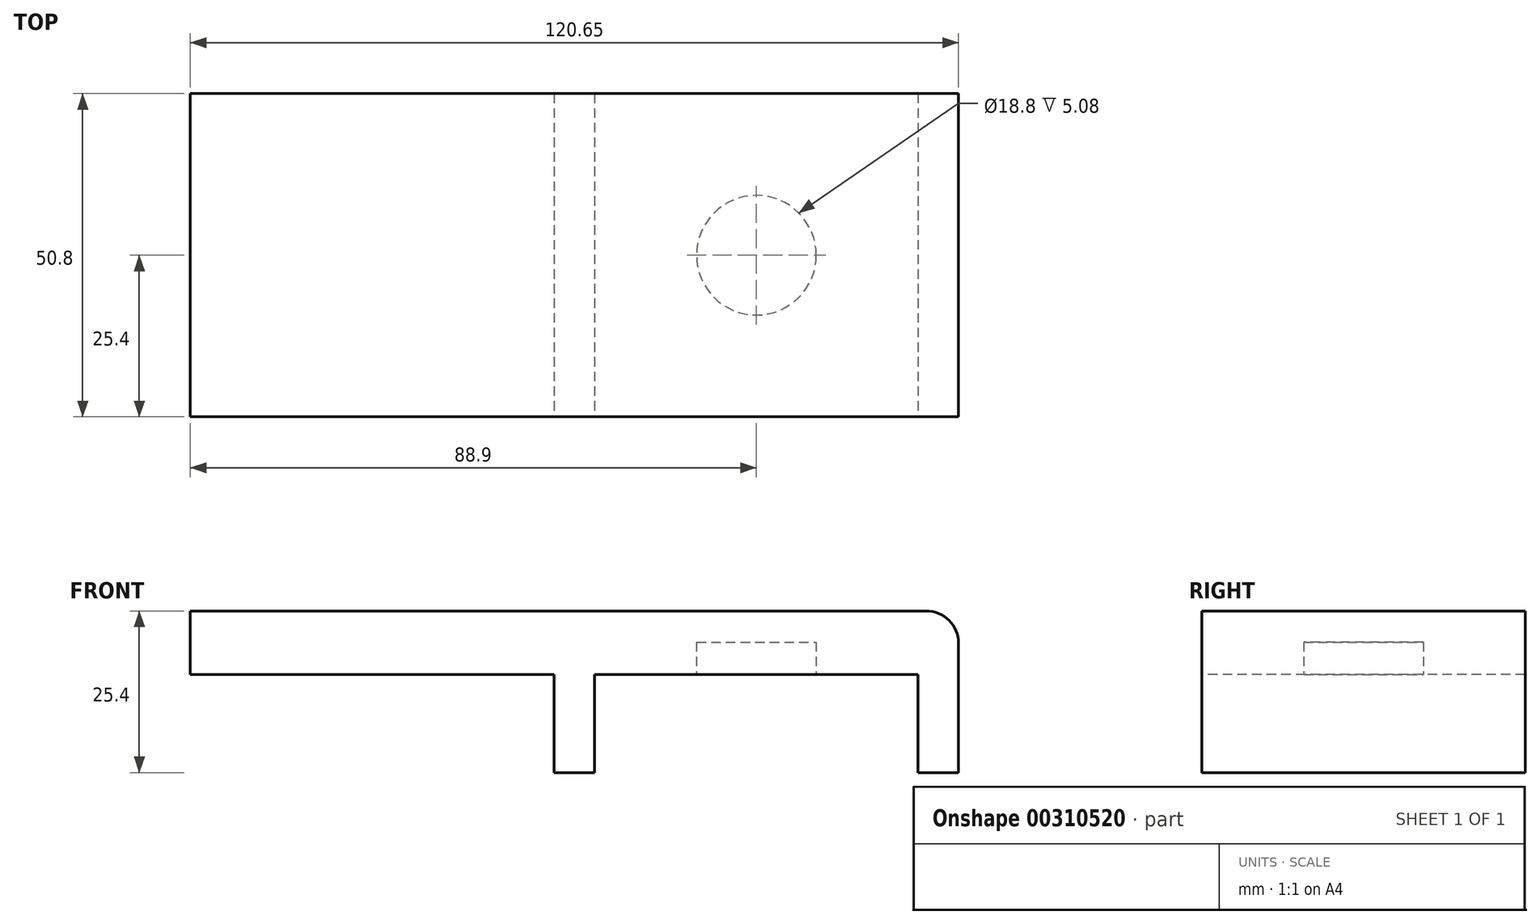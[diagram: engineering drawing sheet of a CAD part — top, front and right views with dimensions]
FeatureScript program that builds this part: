
annotation { "Feature Type Name" : "Feature", "Feature Type Description" : "" }
export const myFeature = defineFeature(function(context is Context, id is Id, definition is map)
    precondition{}
    {
        {
            var Q0;
            Q0=qCreatedBy(makeId("Front.planeOp"),FACE);
            var sketch = newSketch(context, id + "F0", { "sketchPlane" : qUnion([Q0])});
            skLineSegment(sketch, "E0.bottom", {"start": v(0, 0) * mm, "end": v(50.8, 0) * mm});
            skLineSegment(sketch, "E0.left", {"start": v(0, 0) * mm, "end": v(0, -15.44) * mm});
            skLineSegment(sketch, "E0.right", {"start": v(50.8, 0) * mm, "end": v(50.8, -15.44) * mm});
            skLineSegment(sketch, "E1.top", {"start": v(0, 9.96) * mm, "end": v(50.8, 9.96) * mm});
            skLineSegment(sketch, "E2.bottom", {"start": v(50.8, 9.96) * mm, "end": v(57.15, 9.96) * mm});
            skLineSegment(sketch, "E2.top", {"start": v(50.8, -15.44) * mm, "end": v(57.15, -15.44) * mm});
            skLineSegment(sketch, "E2.right", {"start": v(57.15, 9.96) * mm, "end": v(57.15, -15.44) * mm});
            skLineSegment(sketch, "E3.bottom", {"start": v(0, 9.96) * mm, "end": v(-6.35, 9.96) * mm});
            skLineSegment(sketch, "E3.top", {"start": v(0, -15.44) * mm, "end": v(-6.35, -15.44) * mm});
            skLineSegment(sketch, "E3.right", {"start": v(-6.35, 0) * mm, "end": v(-6.35, -15.44) * mm});
            skLineSegment(sketch, "E4", {"start": v(-6.35, 9.96) * mm, "end": v(-63.5, 9.96) * mm});
            skLineSegment(sketch, "E5", {"start": v(-63.5, 9.96) * mm, "end": v(-63.5, -0.04) * mm});
            skLineSegment(sketch, "E6", {"start": v(-63.5, -0.04) * mm, "end": v(-6.35, 0) * mm});
            skSolve(sketch);
        }
        {
            var Q0;
            Q0=makeQuery(id+"F0.imprint","IMPRINT",FACE,{"disambiguationData":[TD([[makeQuery(id+"F0.imprint","IMPRINT",EDGE,{"derivedFrom":sQuery(id+"F0.wireOp",EDGE,"E0.bottom")}),1.0]])]});
            extrude(context, id + "F1", {"entities" : qUnion([Q0]), "oppositeDirection" : true, "depth" : 50.8 * mm});
        }
        {
            var Q0;
            Q0=makeQuery(id+"F1.opExtrude","SWEPT_EDGE",EDGE,{"disambiguationData":[OSD([sQuery(id+"F0.wireOp",EDGE,"E2.bottom"),sQuery(id+"F0.wireOp",EDGE,"E2.right")])]});
            fillet(context, id + "F2", {"entities" : qUnion([Q0]), "radius" : 5.08 * mm, "tangentPropagation" : true, "allowEdgeOverflow" : false});
        }
        {
            var Q0;
            Q0=makeQuery(id+"F1.opExtrude","SWEPT_FACE",FACE,{"disambiguationData":[OSD([sQuery(id+"F0.wireOp",EDGE,"E0.bottom")])]});
            var sketch = newSketch(context, id + "F3", { "sketchPlane" : qUnion([Q0])});
            skLineSegment(sketch, "E7", {"start": v(0, 0) * mm, "end": v(50.8, -50.8) * mm, "construction": true});
            skLineSegment(sketch, "E8", {"start": v(0, -50.8) * mm, "end": v(50.8, 0) * mm, "construction": true});
            skCircle(sketch, "E9", {"center": v(25.4, -25.4) * mm, "radius": 9.4 * mm});
            skSolve(sketch);
        }
        {
            var Q0;
            Q0=makeQuery(id+"F3.imprint","IMPRINT",FACE,{"disambiguationData":[TD([[makeQuery(id+"F3.imprint","IMPRINT",EDGE,{"derivedFrom":sQuery(id+"F3.wireOp",EDGE,"E9")}),1.0]])]});
            extrude(context, id + "F4", {"entities" : qUnion([Q0]), "operationType" : NewBodyOperationType.REMOVE, "oppositeDirection" : true, "depth" : 5.08 * mm});
        }
    });
